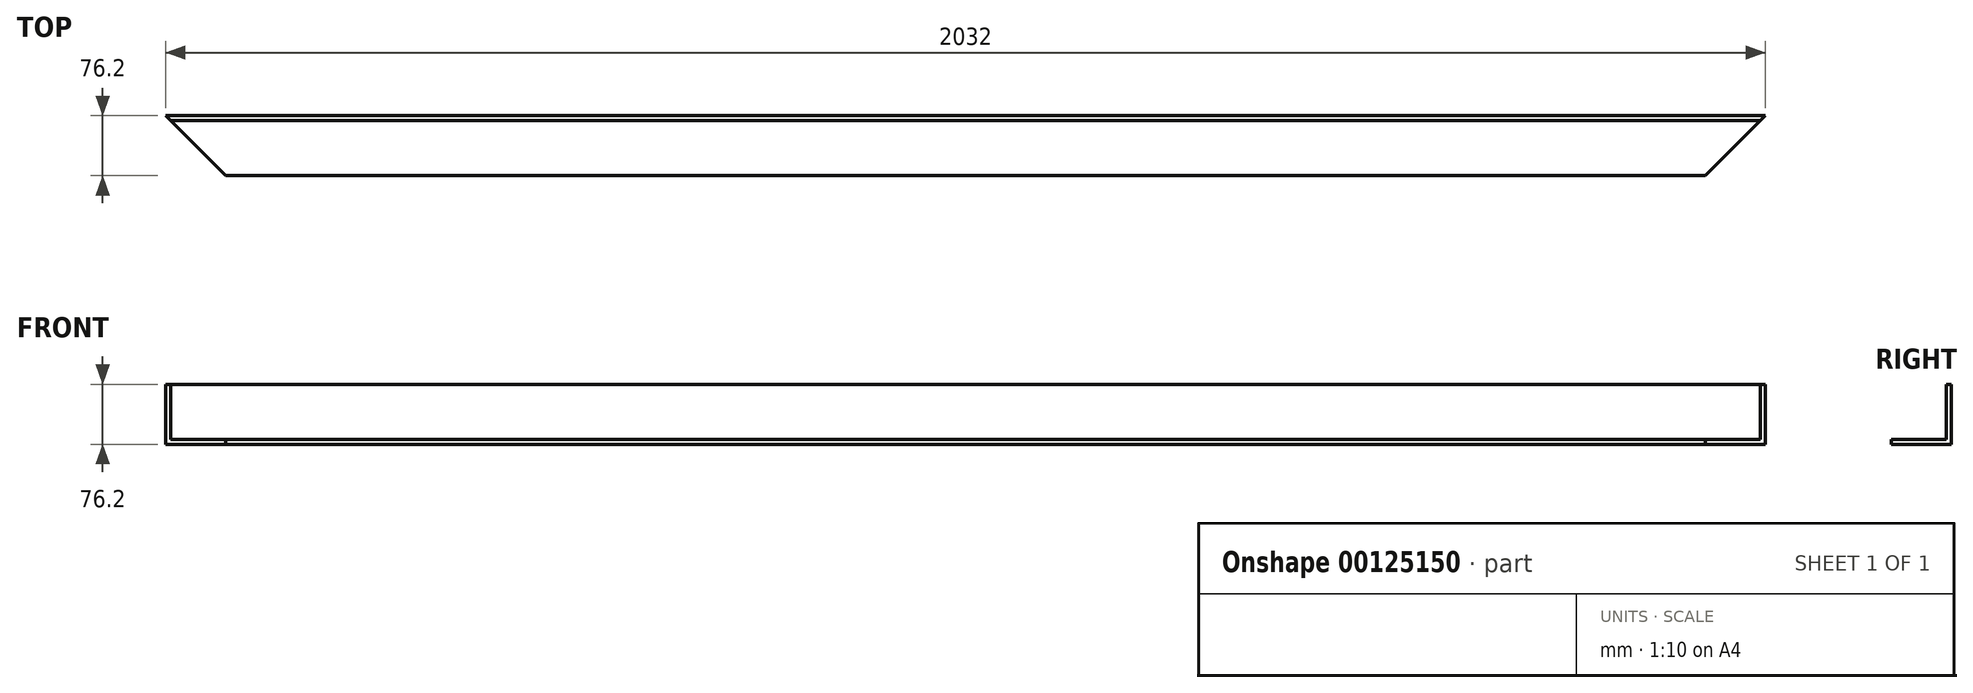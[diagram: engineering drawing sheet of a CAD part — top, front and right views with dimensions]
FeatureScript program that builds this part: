
annotation { "Feature Type Name" : "Feature", "Feature Type Description" : "" }
export const myFeature = defineFeature(function(context is Context, id is Id, definition is map)
    precondition{}
    {
        {
            var Q0;
            Q0=qCreatedBy(makeId("Top.planeOp"),FACE);
            var sketch = newSketch(context, id + "F0", { "sketchPlane" : qUnion([Q0])});
            skLineSegment(sketch, "E0", {"start": v(0, 0) * mm, "end": v(-2032, 0) * mm});
            skLineSegment(sketch, "E1.0", {"start": v(0, 76.2) * mm, "end": v(-2032, 76.2) * mm});
            skLineSegment(sketch, "E2", {"start": v(-2032, 76.2) * mm, "end": v(-2032, 0) * mm});
            skLineSegment(sketch, "E3", {"start": v(0, 76.2) * mm, "end": v(0, 0) * mm});
            skSolve(sketch);
        }
        {
            var Q0;
            Q0=qSketchRegion(id+"F0",true);
            extrude(context, id + "F1", {"entities" : qUnion([Q0]), "oppositeDirection" : true, "depth" : 76.2 * mm});
        }
        {
            var Q0;
            Q0=makeQuery(id+"F1.opExtrude","CAP_FACE",FACE,{"disambiguationData":[OSD([sQuery(id+"F0.wireOp",EDGE,"E0"),sQuery(id+"F0.wireOp",EDGE,"E1.0"),sQuery(id+"F0.wireOp",EDGE,"E2"),sQuery(id+"F0.wireOp",EDGE,"E3")])],"isStart":true});
            var sketch = newSketch(context, id + "F2", { "sketchPlane" : qUnion([Q0])});
            skLineSegment(sketch, "E4.2", {"start": v(0, 0) * mm, "end": v(-2032, 0) * mm});
            skLineSegment(sketch, "E5.0", {"start": v(0, 69.85) * mm, "end": v(-2032, 69.85) * mm});
            skLineSegment(sketch, "E6", {"start": v(-2032, 69.85) * mm, "end": v(-2032, 0) * mm});
            skLineSegment(sketch, "E7", {"start": v(0, 69.85) * mm, "end": v(0, 0) * mm});
            skSolve(sketch);
        }
        {
            var Q0;
            Q0=qSketchRegion(id+"F2",true);
            extrude(context, id + "F3", {"entities" : qUnion([Q0]), "operationType" : NewBodyOperationType.REMOVE, "oppositeDirection" : true, "depth" : 69.85 * mm});
        }
        {
            var Q0;
            Q0=makeQuery(id+"F1.opExtrude","CAP_FACE",FACE,{"disambiguationData":[OSD([sQuery(id+"F0.wireOp",EDGE,"E0"),sQuery(id+"F0.wireOp",EDGE,"E1.0"),sQuery(id+"F0.wireOp",EDGE,"E2"),sQuery(id+"F0.wireOp",EDGE,"E3")])],"isStart":true});
            var sketch = newSketch(context, id + "F4", { "sketchPlane" : qUnion([Q0])});
            skLineSegment(sketch, "E8", {"start": v(-2032, 76.2) * mm, "end": v(-1955.8, 0) * mm});
            skLineSegment(sketch, "E9", {"start": v(-76.2, 0) * mm, "end": v(0, 76.2) * mm});
            skLineSegment(sketch, "E10", {"start": v(-76.2, 0) * mm, "end": v(0, 0) * mm});
            skLineSegment(sketch, "E11", {"start": v(0, 0) * mm, "end": v(0, 76.2) * mm});
            skLineSegment(sketch, "E12", {"start": v(-1955.8, 0) * mm, "end": v(-2032, 0) * mm});
            skLineSegment(sketch, "E13", {"start": v(-2032, 0) * mm, "end": v(-2032, 76.2) * mm});
            skSolve(sketch);
        }
        {
            var Q0;
            Q0=qSketchRegion(id+"F4",true);
            extrude(context, id + "F5", {"entities" : qUnion([Q0]), "operationType" : NewBodyOperationType.REMOVE, "oppositeDirection" : true, "depth" : 76.2 * mm});
        }
    });
